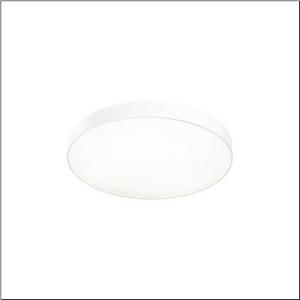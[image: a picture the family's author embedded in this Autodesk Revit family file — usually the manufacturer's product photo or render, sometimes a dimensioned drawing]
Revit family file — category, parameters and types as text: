
# Revit family: round_21_m_51mr36fd0421w
name_source: partatom
category: Lighting Fixtures
units: mm (PartAtom-declared; Revit-internal decimal feet)

## family parameters
Cut with Voids When Loaded = No
Host = Face
Light Source = No
Part Type = Normal
Room Calculation Point = No
Round Connector Dimension = Use Diameter
Shared = No

## types (1)
- Round 21 M (1 x LED, 7810 lm, 54.9 W, 4000K)
    Apparent Load = 55 VA
    CIE Flux Codes = 49 80 96 100 100
    Color Rendering = 80
    Color Temperature = 4000K
    Default Elevation = 1800 mm
    Description = Round 21 M, wall and ceiling luminaire, primary optical cover: cover, of PMMA, opal, light emission: direct distribution, primary light characteristic: symmetric, installation type: surface-mounted, suspended mounting, LED, rated luminous flux: 7.810lm, luminous efficacy: 142lm/W, light colour: 840, colour temperature: 4000K, control gear: DALI 2, with terminal, 5-pole, mains connection: 230V, AC, 50/60Hz, rated input power: 55W, housing, of aluminium, coated, white, diameter: 600mm, height: 62mm, protection rating (complete): IP40, insulation class (complete): insulation class I (protective earthing), certification: CE, impact resistance: IK04, permissible operating ambient temperature: -10..+35°C, packaging unit: 1 piece
    Height = 87 mm
    Lamp = 1 x LED
    Lamp Light Flux = 7810 lm
    Lamp Power = 54.9 W
    Lamp count = 1
    Length = 600 mm
    Luminous efficacy = 142 lm/W
    Manufacturer = Siteco
    ModVariant = No
    Model = 51MR36FD0421W
    Mounting Place = Ceiling
    Mounting Type = Surface mounted
    Number of Poles = 1
    OnlyDefault = Yes
    Power Factor = 1
    Product Name = Round 21 M
    Product group = wall and ceiling luminaire
    ProductGroupID = 304
    Protection Class = Protection class I
    Protection Degree = IP 40
    RLX_Detail_Level = 1
    RLX_Emergency_Light_Flux = 0 lm
    RLX_Emergency_Type = 0
    RLX_Emergency_Type_DB = No
    RlxData = <blob elided: 11713 chars, md5=c17d44de>
    Socket = socket
    Standby Power = 0 W
    System Light Flux = 7810 lm
    System Power = 55 W
    Type Comments = Product without accessories
    Type Image = l_1258330.jpg
    URL = http://relux.com
    VarID = ---
    Voltage = 0 V
    Weight = 0.00 kg
    Width = 0 mm  [stored 0 ft]

note: [stored X ft] marks values corroborated as IEEE doubles in the binary element streams (Revit-internal decimal feet)

## geometry (parser evidence)
native form markers: Sweep x9
no freeform markers — native parametric forms only
